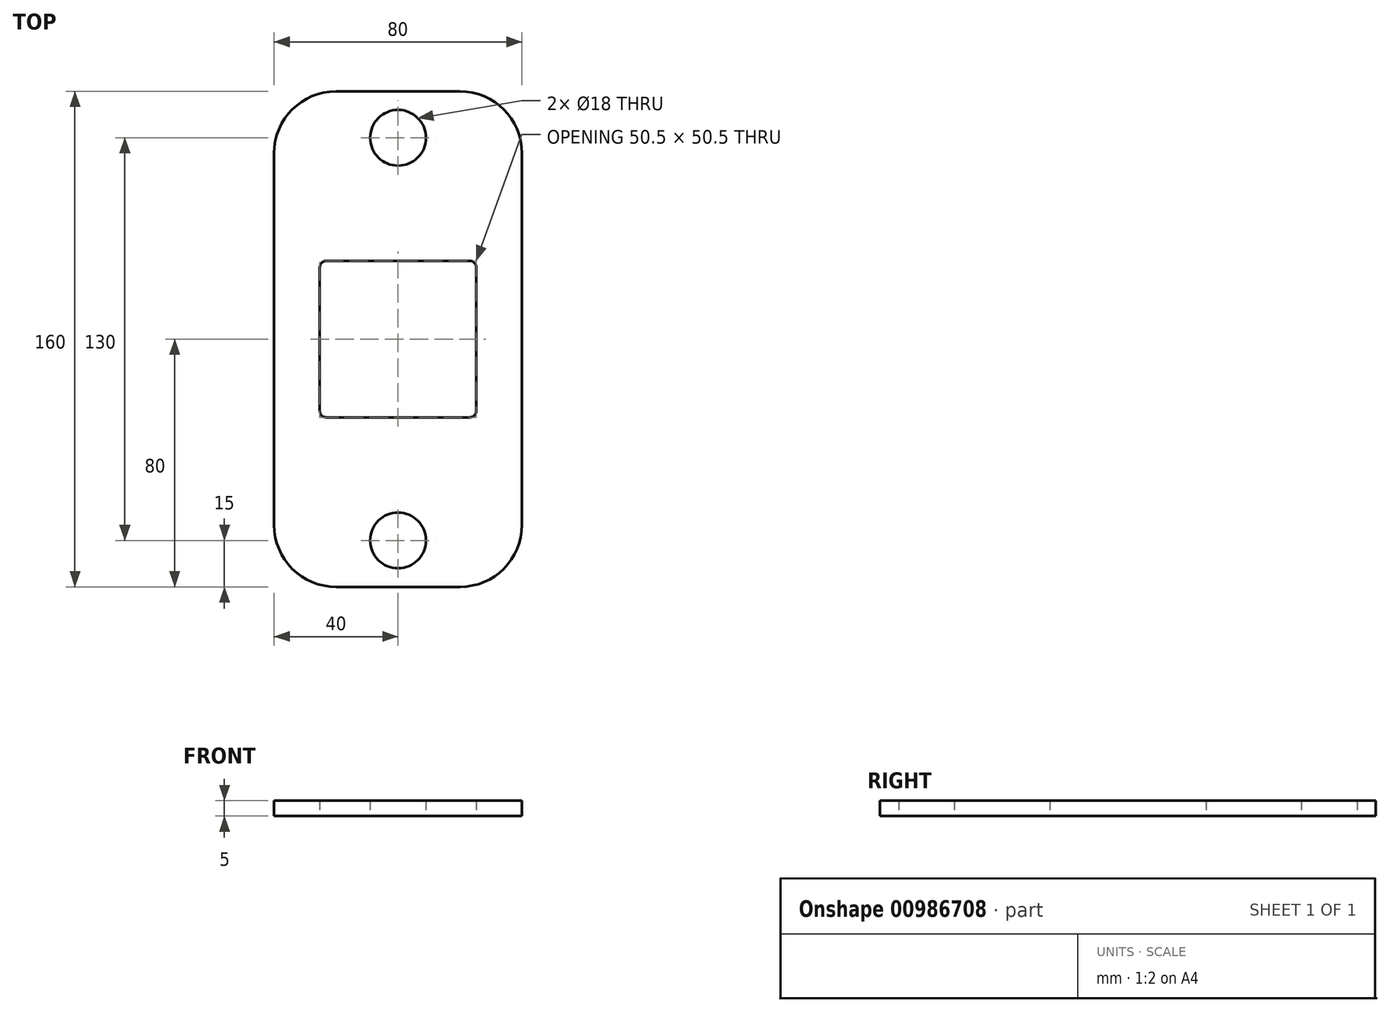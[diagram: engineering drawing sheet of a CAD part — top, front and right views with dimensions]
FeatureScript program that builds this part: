
annotation { "Feature Type Name" : "Feature", "Feature Type Description" : "" }
export const myFeature = defineFeature(function(context is Context, id is Id, definition is map)
    precondition{}
    {
        {
            var Q0;
            Q0=qCreatedBy(makeId("Top.planeOp"),FACE);
            var sketch = newSketch(context, id + "F0", { "sketchPlane" : qUnion([Q0])});
            skLineSegment(sketch, "E0.bottom", {"start": v(23.25, -25.25) * mm, "end": v(-23.25, -25.25) * mm});
            skLineSegment(sketch, "E0.top", {"start": v(23.25, 25.25) * mm, "end": v(-23.25, 25.25) * mm});
            skLineSegment(sketch, "E0.left", {"start": v(25.25, -23.25) * mm, "end": v(25.25, 23.25) * mm});
            skLineSegment(sketch, "E0.right", {"start": v(-25.25, -23.25) * mm, "end": v(-25.25, 23.25) * mm});
            skPoint(sketch, "E0.middle", {"position": v(0, 0) * mm});
            skPoint(sketch, "E1.visualSharp", {"position": v(-25.25, 25.25) * mm});
            skArc(sketch, "E1.filletArc", {"start": v(-23.25, 25.25) * mm, "mid": v(-24.66, 24.66) * mm, "end": v(-25.25, 23.25) * mm});
            skPoint(sketch, "E2.visualSharp", {"position": v(-25.25, -25.25) * mm});
            skArc(sketch, "E2.filletArc", {"start": v(-25.25, -23.25) * mm, "mid": v(-24.66, -24.66) * mm, "end": v(-23.25, -25.25) * mm});
            skPoint(sketch, "E3.visualSharp", {"position": v(25.25, -25.25) * mm});
            skArc(sketch, "E3.filletArc", {"start": v(23.25, -25.25) * mm, "mid": v(24.66, -24.66) * mm, "end": v(25.25, -23.25) * mm});
            skPoint(sketch, "E4.visualSharp", {"position": v(25.25, 25.25) * mm});
            skArc(sketch, "E4.filletArc", {"start": v(25.25, 23.25) * mm, "mid": v(24.66, 24.66) * mm, "end": v(23.25, 25.25) * mm});
            skCircle(sketch, "E5", {"center": v(0, 0) * mm, "radius": 35.5 * mm, "construction": true});
            skPoint(sketch, "E6.endSnap0", {"position": v(0, 25.25) * mm});
            skLineSegment(sketch, "E7", {"start": v(0, 80) * mm, "end": v(-20, 80) * mm});
            skLineSegment(sketch, "E8", {"start": v(-40, 60) * mm, "end": v(-40, -60) * mm});
            skLineSegment(sketch, "E9", {"start": v(-20, -80) * mm, "end": v(20, -80) * mm});
            skLineSegment(sketch, "E10", {"start": v(40, -60) * mm, "end": v(40, 60) * mm});
            skLineSegment(sketch, "E11", {"start": v(20, 80) * mm, "end": v(0, 80) * mm});
            skLineSegment(sketch, "E12", {"start": v(0, 0) * mm, "end": v(0, 80) * mm, "construction": true});
            skLineSegment(sketch, "E13", {"start": v(0, -80) * mm, "end": v(0, -65) * mm, "construction": true});
            skCircle(sketch, "E14", {"center": v(0, -65) * mm, "radius": 9 * mm});
            skLineSegment(sketch, "E15", {"start": v(0, 80) * mm, "end": v(0, 65) * mm});
            skCircle(sketch, "E16", {"center": v(0, 65) * mm, "radius": 9 * mm});
            skPoint(sketch, "E17.visualSharp", {"position": v(-40, -80) * mm});
            skArc(sketch, "E17.filletArc", {"start": v(-40, -60) * mm, "mid": v(-34.14, -74.14) * mm, "end": v(-20, -80) * mm});
            skPoint(sketch, "E18.visualSharp", {"position": v(40, -80) * mm});
            skArc(sketch, "E18.filletArc", {"start": v(20, -80) * mm, "mid": v(34.14, -74.14) * mm, "end": v(40, -60) * mm});
            skPoint(sketch, "E19.visualSharp", {"position": v(40, 80) * mm});
            skArc(sketch, "E19.filletArc", {"start": v(40, 60) * mm, "mid": v(34.14, 74.14) * mm, "end": v(20, 80) * mm});
            skPoint(sketch, "E20.visualSharp", {"position": v(-40, 80) * mm});
            skArc(sketch, "E20.filletArc", {"start": v(-20, 80) * mm, "mid": v(-34.14, 74.14) * mm, "end": v(-40, 60) * mm});
            skSolve(sketch);
        }
        {
            var Q0;
            Q0=makeQuery(id+"F0.imprint","IMPRINT",FACE,{"disambiguationData":[TD([[makeQuery(id+"F0.imprint","IMPRINT",EDGE,{"derivedFrom":sQuery(id+"F0.wireOp",EDGE,"E0.bottom")}),1.0]])]});
            extrude(context, id + "F1", {"entities" : qUnion([Q0]), "depth" : 5 * mm, "offsetDistance" : 25 * mm});
        }
    });
